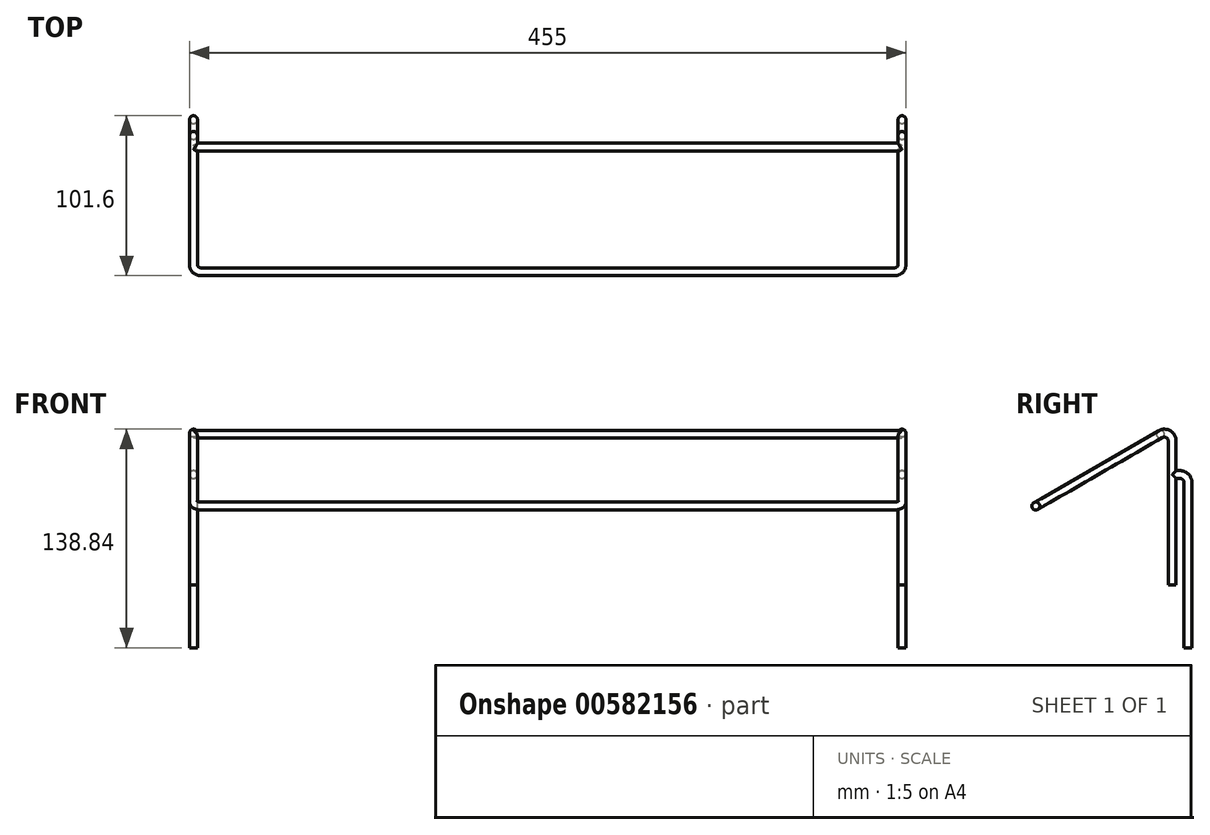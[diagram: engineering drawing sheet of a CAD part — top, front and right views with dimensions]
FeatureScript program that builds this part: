
annotation { "Feature Type Name" : "Feature", "Feature Type Description" : "" }
export const myFeature = defineFeature(function(context is Context, id is Id, definition is map)
    precondition{}
    {
        {
            var Q0;
            Q0=qCreatedBy(makeId("Right.planeOp"),FACE);
            cPlane(context, id + "F0", {"entities" : qUnion([Q0]), "cplaneType" : CPlaneType.OFFSET, "offset" : 450 * mm, "oppositeDirection" : true, "width" : 150 * mm, "height" : 150 * mm});
        }
        {
            var Q0;
            Q0=qCreatedBy(makeId("Top.planeOp"),FACE);
            var sketch = newSketch(context, id + "F1", { "sketchPlane" : qUnion([Q0])});
            skLineSegment(sketch, "E0", {"start": v(0, 0) * mm, "end": v(-450, 0) * mm});
            skSolve(sketch);
        }
        {
            var Q0;
            Q0=qCreatedBy(makeId("Top.planeOp"),FACE);
            var Q1;
            Q1=sQuery(id+"F1.wireOp",EDGE,"E0");
            cPlane(context, id + "F2", {"entities" : qUnion([Q0, Q1]), "cplaneType" : CPlaneType.LINE_ANGLE, "offset" : 25 * mm, "angle" : 150 * degree, "width" : 150 * mm, "height" : 150 * mm});
        }
        {
            var Q0;
            Q0=qCreatedBy(makeId("Right.planeOp"),FACE);
            var sketch = newSketch(context, id + "F3", { "sketchPlane" : qUnion([Q0])});
            skLineSegment(sketch, "E1", {"start": v(0, -8.66) * mm, "end": v(0, -100) * mm});
            skLineSegment(sketch, "E2", {"start": v(-7.5, -4.33) * mm, "end": v(-43.3, -25) * mm});
            skLineSegment(sketch, "E3", {"start": v(0, -30) * mm, "end": v(5, -30) * mm});
            skLineSegment(sketch, "E4", {"start": v(10, -35) * mm, "end": v(10, -140) * mm});
            skPoint(sketch, "E5.visualSharp", {"position": v(0, 0) * mm});
            skArc(sketch, "E5.filletArc", {"start": v(0, -8.66) * mm, "mid": v(-2.5, -4.33) * mm, "end": v(-7.5, -4.33) * mm});
            skPoint(sketch, "E6.visualSharp", {"position": v(10, -30) * mm});
            skArc(sketch, "E6.filletArc", {"start": v(10, -35) * mm, "mid": v(8.54, -31.46) * mm, "end": v(5, -30) * mm});
            skSolve(sketch);
        }
        {
            var Q0;
            Q0=qCreatedBy(id+"F0.planeOp",FACE);
            var sketch = newSketch(context, id + "F4", { "sketchPlane" : qUnion([Q0])});
            skLineSegment(sketch, "E7", {"start": v(0, -8.66) * mm, "end": v(0, -100) * mm});
            skLineSegment(sketch, "E8", {"start": v(-7.5, -4.33) * mm, "end": v(-43.3, -25) * mm});
            skLineSegment(sketch, "E9", {"start": v(0, -30) * mm, "end": v(5, -30) * mm});
            skLineSegment(sketch, "E10", {"start": v(10, -35) * mm, "end": v(10, -140) * mm});
            skPoint(sketch, "E11.visualSharp", {"position": v(0, 0) * mm});
            skArc(sketch, "E11.filletArc", {"start": v(0, -8.66) * mm, "mid": v(-2.5, -4.33) * mm, "end": v(-7.5, -4.33) * mm});
            skPoint(sketch, "E12.visualSharp", {"position": v(10, -30) * mm});
            skArc(sketch, "E12.filletArc", {"start": v(10, -35) * mm, "mid": v(8.54, -31.46) * mm, "end": v(5, -30) * mm});
            skSolve(sketch);
        }
        {
            var Q0;
            Q0=qCreatedBy(id+"F2.planeOp",FACE);
            var sketch = newSketch(context, id + "F5", { "sketchPlane" : qUnion([Q0])});
            skLineSegment(sketch, "E13", {"start": v(0, -50) * mm, "end": v(0, -95) * mm});
            skLineSegment(sketch, "E14", {"start": v(-5, -100) * mm, "end": v(-445, -100) * mm});
            skLineSegment(sketch, "E15", {"start": v(-450, -95) * mm, "end": v(-450, -50) * mm});
            skPoint(sketch, "E16.visualSharp", {"position": v(-450, -100) * mm});
            skArc(sketch, "E16.filletArc", {"start": v(-450, -95) * mm, "mid": v(-448.54, -98.54) * mm, "end": v(-445, -100) * mm});
            skPoint(sketch, "E17.visualSharp", {"position": v(0, -100) * mm});
            skArc(sketch, "E17.filletArc", {"start": v(-5, -100) * mm, "mid": v(-1.46, -98.54) * mm, "end": v(0, -95) * mm});
            skLineSegment(sketch, "E18", {"start": v(-450, -8.66) * mm, "end": v(0, -8.66) * mm});
            skSolve(sketch);
        }
        {
            var Q0;
            Q0=qCreatedBy(makeId("Top.planeOp"),FACE);
            var Q1;
            Q1=sQuery(id+"F3.wireOp",VERTEX,"E1.end");
            cPlane(context, id + "F6", {"entities" : qUnion([Q0, Q1]), "cplaneType" : CPlaneType.PLANE_POINT, "offset" : 25 * mm, "width" : 150 * mm, "height" : 150 * mm});
        }
        {
            var Q0;
            Q0=qCreatedBy(id+"F6.planeOp",FACE);
            var Q1;
            Q1=sQuery(id+"F3.wireOp",VERTEX,"E4.end");
            cPlane(context, id + "F7", {"entities" : qUnion([Q0, Q1]), "cplaneType" : CPlaneType.PLANE_POINT, "offset" : 25 * mm, "width" : 150 * mm, "height" : 150 * mm});
        }
        {
            var Q0;
            Q0=qCreatedBy(id+"F7.planeOp",FACE);
            var sketch = newSketch(context, id + "F8", { "sketchPlane" : qUnion([Q0])});
            skCircle(sketch, "E19", {"center": v(0, 10) * mm, "radius": 2.5 * mm});
            skSolve(sketch);
        }
        {
            var Q0;
            Q0=qCreatedBy(id+"F6.planeOp",FACE);
            var sketch = newSketch(context, id + "F9", { "sketchPlane" : qUnion([Q0])});
            skCircle(sketch, "E20", {"center": v(0, 0) * mm, "radius": 2.5 * mm});
            skSolve(sketch);
        }
        {
            var Q0;
            Q0=qCreatedBy(makeId("Right.planeOp"),FACE);
            cPlane(context, id + "F10", {"entities" : qUnion([Q0]), "cplaneType" : CPlaneType.OFFSET, "offset" : 25 * mm, "oppositeDirection" : true, "width" : 150 * mm, "height" : 150 * mm});
        }
        {
            var Q0;
            Q0=qCreatedBy(id+"F10.planeOp",FACE);
            var sketch = newSketch(context, id + "F11", { "sketchPlane" : qUnion([Q0])});
            skCircle(sketch, "E21", {"center": v(-7.5, -4.33) * mm, "radius": 2.5 * mm});
            skSolve(sketch);
        }
        {
            var Q0;
            Q0=makeQuery(id+"F9.imprint","IMPRINT",FACE,{"disambiguationData":[TD([[makeQuery(id+"F9.imprint","IMPRINT",EDGE,{"derivedFrom":sQuery(id+"F9.wireOp",EDGE,"E20")}),1.0]])]});
            var Q1;
            Q1=sQuery(id+"F3.wireOp",EDGE,"E1");
            var Q2;
            Q2=sQuery(id+"F3.wireOp",EDGE,"E5.filletArc");
            var Q3;
            Q3=sQuery(id+"F3.wireOp",EDGE,"E2");
            var Q4;
            Q4=sQuery(id+"F5.wireOp",EDGE,"E13");
            var Q5;
            Q5=sQuery(id+"F5.wireOp",EDGE,"E17.filletArc");
            var Q6;
            Q6=sQuery(id+"F5.wireOp",EDGE,"E14");
            var Q7;
            Q7=sQuery(id+"F5.wireOp",EDGE,"E16.filletArc");
            var Q8;
            Q8=sQuery(id+"F5.wireOp",EDGE,"E15");
            var Q9;
            Q9=sQuery(id+"F4.wireOp",EDGE,"E8");
            var Q10;
            Q10=sQuery(id+"F4.wireOp",EDGE,"E11.filletArc");
            var Q11;
            Q11=sQuery(id+"F4.wireOp",EDGE,"E7");
            sweep(context, id + "F12", {"profiles" : qUnion([Q0]), "path" : qUnion([Q1, Q2, Q3, Q4, Q5, Q6, Q7, Q8, Q9, Q10, Q11])});
        }
        {
            var Q0;
            Q0=makeQuery(id+"F8.imprint","IMPRINT",FACE,{"disambiguationData":[TD([[makeQuery(id+"F8.imprint","IMPRINT",EDGE,{"derivedFrom":sQuery(id+"F8.wireOp",EDGE,"E19")}),1.0]])]});
            var Q1;
            Q1=sQuery(id+"F3.wireOp",EDGE,"E4");
            var Q2;
            Q2=sQuery(id+"F3.wireOp",EDGE,"E6.filletArc");
            var Q3;
            Q3=sQuery(id+"F3.wireOp",EDGE,"E3");
            sweep(context, id + "F13", {"operationType" : NewBodyOperationType.ADD, "profiles" : qUnion([Q0]), "path" : qUnion([Q1, Q2, Q3])});
        }
        {
            var Q0;
            Q0=qCreatedBy(id+"F7.planeOp",FACE);
            var sketch = newSketch(context, id + "F14", { "sketchPlane" : qUnion([Q0])});
            skCircle(sketch, "E22", {"center": v(-450, 10) * mm, "radius": 2.5 * mm});
            skSolve(sketch);
        }
        {
            var Q0;
            Q0=makeQuery(id+"F14.imprint","IMPRINT",FACE,{"disambiguationData":[TD([[makeQuery(id+"F14.imprint","IMPRINT",EDGE,{"derivedFrom":sQuery(id+"F14.wireOp",EDGE,"E22")}),1.0]])]});
            var Q1;
            Q1=sQuery(id+"F4.wireOp",EDGE,"E10");
            var Q2;
            Q2=sQuery(id+"F4.wireOp",EDGE,"E12.filletArc");
            var Q3;
            Q3=sQuery(id+"F4.wireOp",EDGE,"E9");
            sweep(context, id + "F15", {"operationType" : NewBodyOperationType.ADD, "profiles" : qUnion([Q0]), "path" : qUnion([Q1, Q2, Q3])});
        }
        {
            var Q0;
            Q0=makeQuery(id+"F11.imprint","IMPRINT",FACE,{"disambiguationData":[TD([[makeQuery(id+"F11.imprint","IMPRINT",EDGE,{"derivedFrom":sQuery(id+"F11.wireOp",EDGE,"E21")}),1.0]])]});
            var Q1;
            Q1=sQuery(id+"F5.wireOp",EDGE,"E18");
            sweep(context, id + "F16", {"operationType" : NewBodyOperationType.ADD, "profiles" : qUnion([Q0]), "path" : qUnion([Q1])});
        }
    });
